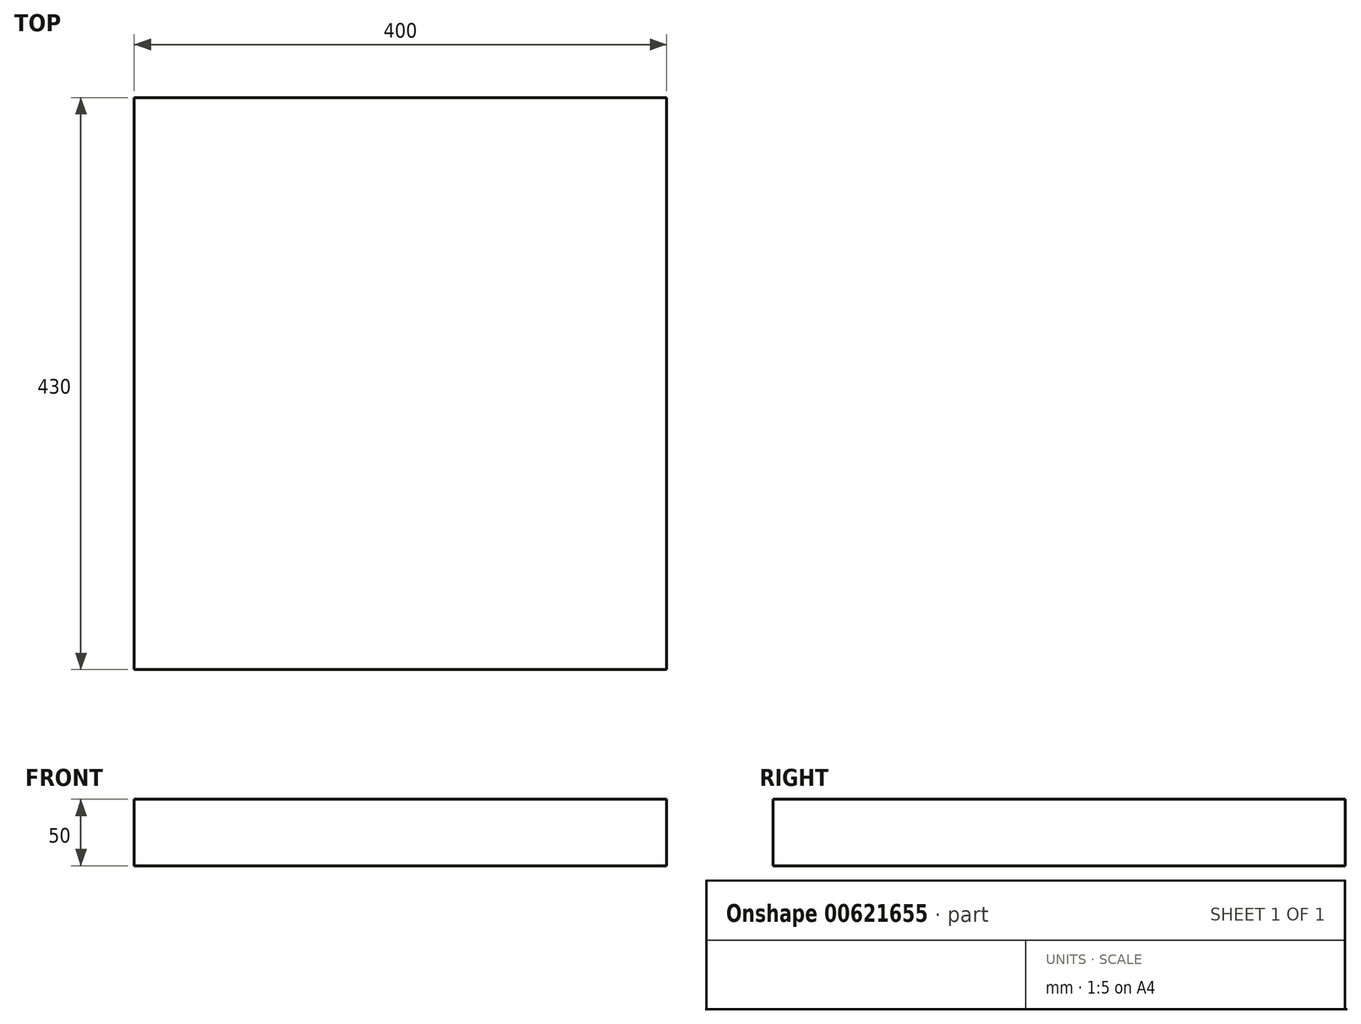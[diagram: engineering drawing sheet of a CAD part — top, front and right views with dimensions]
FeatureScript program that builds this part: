
annotation { "Feature Type Name" : "Feature", "Feature Type Description" : "" }
export const myFeature = defineFeature(function(context is Context, id is Id, definition is map)
    precondition{}
    {
        {
            var Q0;
            Q0=qCreatedBy(makeId("Top.planeOp"),FACE);
            var sketch = newSketch(context, id + "F0", { "sketchPlane" : qUnion([Q0])});
            skLineSegment(sketch, "E0.bottom", {"start": v(0, 0) * mm, "end": v(400, 0) * mm});
            skLineSegment(sketch, "E0.top", {"start": v(0, 430) * mm, "end": v(400, 430) * mm});
            skLineSegment(sketch, "E0.left", {"start": v(0, 0) * mm, "end": v(0, 430) * mm});
            skLineSegment(sketch, "E0.right", {"start": v(400, 0) * mm, "end": v(400, 430) * mm});
            skSolve(sketch);
        }
        {
            var Q0;
            Q0 = qSketchRegion(id + "F0", true);
            extrude(context, id + "F1", {"entities" : qUnion([Q0]), "depth" : 50 * mm, "offsetDistance" : 25 * mm});
        }
    });
